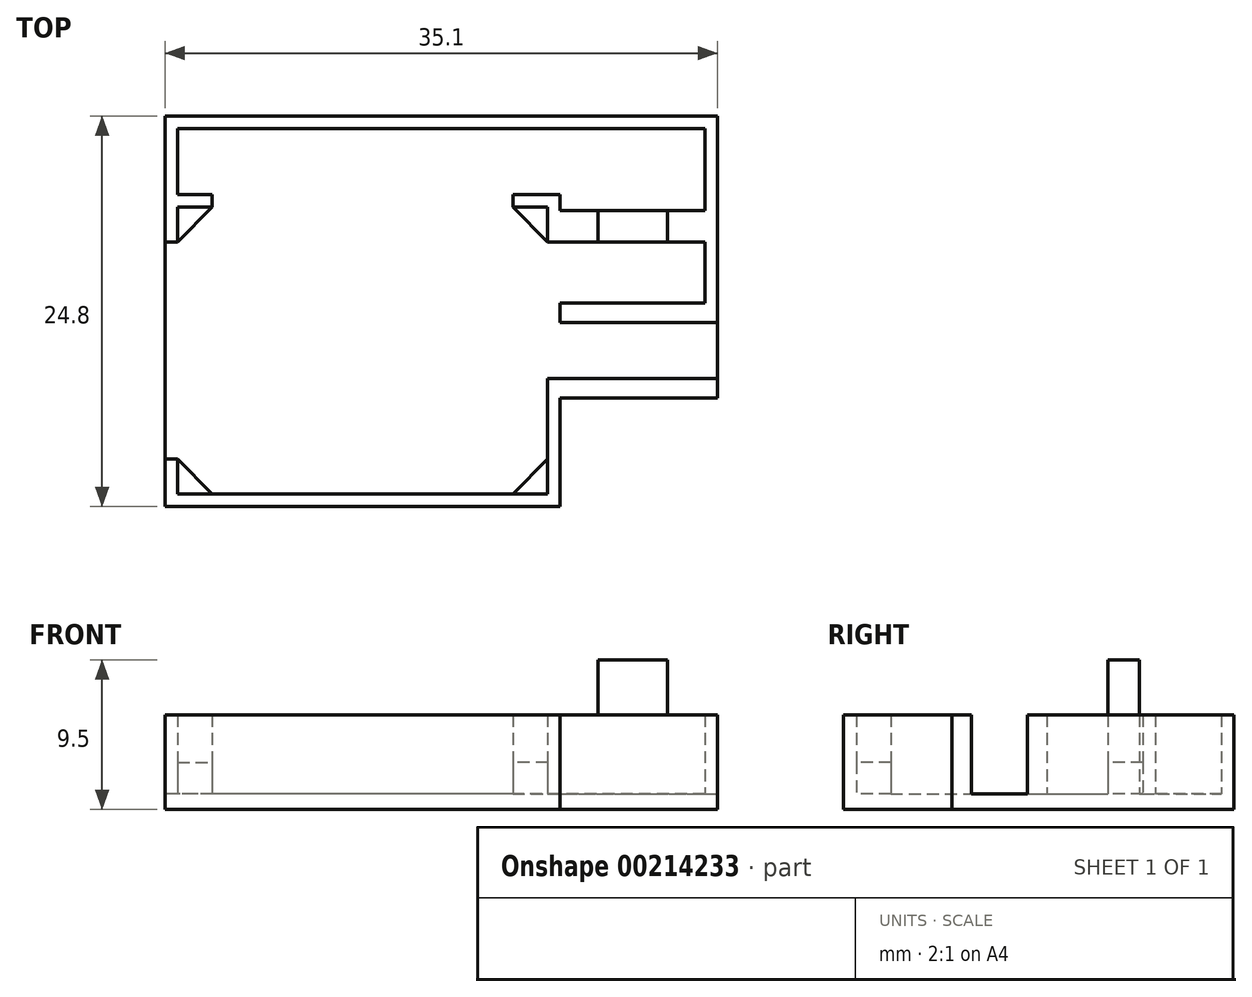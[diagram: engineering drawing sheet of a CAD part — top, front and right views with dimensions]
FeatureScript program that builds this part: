
annotation { "Feature Type Name" : "Feature", "Feature Type Description" : "" }
export const myFeature = defineFeature(function(context is Context, id is Id, definition is map)
    precondition{}
    {
        {
            var Q0;
            Q0=qCreatedBy(makeId("Top.planeOp"),FACE);
            var sketch = newSketch(context, id + "F0", { "sketchPlane" : qUnion([Q0])});
            skLineSegment(sketch, "E0.bottom", {"start": v(23.18, -7.6) * mm, "end": v(-1.92, -7.6) * mm});
            skLineSegment(sketch, "E0.top", {"start": v(23.18, 12.2) * mm, "end": v(-1.92, 12.2) * mm});
            skLineSegment(sketch, "E0.left", {"start": v(23.18, -7.6) * mm, "end": v(23.18, 12.2) * mm});
            skLineSegment(sketch, "E0.right", {"start": v(-1.92, -7.6) * mm, "end": v(-1.92, -6.8) * mm});
            skPoint(sketch, "E0.middle", {"position": v(10.63, 2.3) * mm});
            skLineSegment(sketch, "E1.bottom", {"start": v(22.38, -6.8) * mm, "end": v(-1.12, -6.8) * mm});
            skLineSegment(sketch, "E1.top", {"start": v(22.38, 11.4) * mm, "end": v(-1.12, 11.4) * mm});
            skLineSegment(sketch, "E1.left", {"start": v(22.38, -6.8) * mm, "end": v(22.38, 11.4) * mm});
            skLineSegment(sketch, "E1.right", {"start": v(-1.12, -6.8) * mm, "end": v(-1.12, 11.4) * mm});
            skLineSegment(sketch, "E2", {"start": v(22.38, 9.2) * mm, "end": v(23.18, 9.2) * mm});
            skLineSegment(sketch, "E3.MirrorCS", {"start": v(22.38, -4.6) * mm, "end": v(23.18, -4.6) * mm});
            skLineSegment(sketch, "E4", {"start": v(-1.12, 9.2) * mm, "end": v(-1.92, 9.2) * mm});
            skPoint(sketch, "E5.MirrorCS.end.orphan", {"position": v(20.18, -7.6) * mm});
            skPoint(sketch, "E5.MirrorCS.start.orphan", {"position": v(20.18, -6.8) * mm});
            skPoint(sketch, "E6.MirrorCS.end.orphan", {"position": v(1.08, -7.6) * mm});
            skPoint(sketch, "E6.MirrorCS.start.orphan", {"position": v(1.08, -6.8) * mm});
            skPoint(sketch, "E7.MirrorCS.end.orphan", {"position": v(1.08, 12.2) * mm});
            skPoint(sketch, "E7.MirrorCS.start.orphan", {"position": v(1.08, 11.4) * mm});
            skPoint(sketch, "E8.end.orphan", {"position": v(20.18, 12.2) * mm});
            skPoint(sketch, "E8.start.orphan", {"position": v(20.18, 11.4) * mm});
            skLineSegment(sketch, "E9", {"start": v(20.18, 11.4) * mm, "end": v(22.38, 9.2) * mm});
            skLineSegment(sketch, "E10", {"start": v(-1.12, -4.6) * mm, "end": v(1.08, -6.8) * mm});
            skLineSegment(sketch, "E11", {"start": v(-1.12, 9.2) * mm, "end": v(1.08, 11.4) * mm});
            skLineSegment(sketch, "E12", {"start": v(22.38, -4.6) * mm, "end": v(20.18, -6.8) * mm});
            skLineSegment(sketch, "E13", {"start": v(1.08, -7.6) * mm, "end": v(1.08, -6.8) * mm});
            skLineSegment(sketch, "E14", {"start": v(20.18, -7.6) * mm, "end": v(20.18, -6.8) * mm});
            skLineSegment(sketch, "E15", {"start": v(1.08, 11.4) * mm, "end": v(1.08, 12.2) * mm});
            skLineSegment(sketch, "E16", {"start": v(20.18, 11.4) * mm, "end": v(20.18, 12.2) * mm});
            skLineSegment(sketch, "E17", {"start": v(10.63, 4.67) * mm, "end": v(10.63, -1.07) * mm, "construction": true});
            skLineSegment(sketch, "E18.MirrorCS", {"start": v(33.18, 12.2) * mm, "end": v(29.93, 12.2) * mm});
            skLineSegment(sketch, "E19.MirrorCS", {"start": v(25.63, 5.32) * mm, "end": v(29.93, 5.32) * mm});
            skLineSegment(sketch, "E20.MirrorCS", {"start": v(23.18, 4.07) * mm, "end": v(32.38, 4.07) * mm});
            skLineSegment(sketch, "E21.MirrorCS", {"start": v(23.18, 0.52) * mm, "end": v(32.38, 0.52) * mm});
            skLineSegment(sketch, "E22.MirrorCS", {"start": v(23.18, -0.73) * mm, "end": v(32.38, -0.73) * mm});
            skLineSegment(sketch, "E23.MirrorCS", {"start": v(32.38, 4.07) * mm, "end": v(33.18, 4.07) * mm});
            skLineSegment(sketch, "E24.MirrorCS", {"start": v(32.38, 0.52) * mm, "end": v(33.18, 0.52) * mm});
            skLineSegment(sketch, "E25.MirrorCS", {"start": v(33.18, 0.52) * mm, "end": v(33.18, 4.07) * mm});
            skLineSegment(sketch, "E26.MirrorCS", {"start": v(33.18, -0.73) * mm, "end": v(33.18, 5.32) * mm});
            skLineSegment(sketch, "E27", {"start": v(33.18, 12.2) * mm, "end": v(33.18, 5.32) * mm});
            skLineSegment(sketch, "E28", {"start": v(33.18, -0.73) * mm, "end": v(32.38, -0.73) * mm});
            skLineSegment(sketch, "E29.trimOffspring", {"start": v(-1.92, 9.2) * mm, "end": v(-1.92, 12.2) * mm});
            skLineSegment(sketch, "E30", {"start": v(-1.92, -6.8) * mm, "end": v(-1.92, 9.2) * mm});
            skLineSegment(sketch, "E31", {"start": v(-1.12, -4.6) * mm, "end": v(-1.92, -4.6) * mm});
            skLineSegment(sketch, "E32", {"start": v(29.93, 12.2) * mm, "end": v(29.93, 5.32) * mm});
            skLineSegment(sketch, "E33", {"start": v(25.63, 5.32) * mm, "end": v(25.63, 12.2) * mm});
            skLineSegment(sketch, "E34", {"start": v(25.63, 5.32) * mm, "end": v(23.18, 5.32) * mm});
            skLineSegment(sketch, "E35", {"start": v(32.38, -0.73) * mm, "end": v(32.38, 12.2) * mm});
            skLineSegment(sketch, "E36", {"start": v(29.93, 5.32) * mm, "end": v(32.38, 5.32) * mm});
            skLineSegment(sketch, "E37", {"start": v(32.38, 5.32) * mm, "end": v(33.18, 5.32) * mm});
            skLineSegment(sketch, "E38", {"start": v(23.18, 11.2) * mm, "end": v(25.63, 11.2) * mm});
            skLineSegment(sketch, "E39", {"start": v(23.18, 9.2) * mm, "end": v(25.63, 9.2) * mm});
            skLineSegment(sketch, "E40.trimOffspring", {"start": v(25.63, 12.2) * mm, "end": v(23.18, 12.2) * mm});
            skLineSegment(sketch, "E41", {"start": v(25.63, 11.2) * mm, "end": v(29.93, 11.2) * mm});
            skLineSegment(sketch, "E42", {"start": v(25.63, 9.2) * mm, "end": v(29.93, 9.2) * mm});
            skLineSegment(sketch, "E43", {"start": v(25.63, 12.2) * mm, "end": v(29.93, 12.2) * mm});
            skLineSegment(sketch, "E44.0", {"start": v(23.18, 17.2) * mm, "end": v(-1.92, 17.2) * mm});
            skLineSegment(sketch, "E44.1", {"start": v(25.63, 17.2) * mm, "end": v(23.18, 17.2) * mm});
            skLineSegment(sketch, "E44.2", {"start": v(25.63, 17.2) * mm, "end": v(29.93, 17.2) * mm});
            skLineSegment(sketch, "E44.3", {"start": v(33.18, 17.2) * mm, "end": v(29.93, 17.2) * mm});
            skLineSegment(sketch, "E45", {"start": v(-1.92, 17.2) * mm, "end": v(-1.92, 12.2) * mm});
            skLineSegment(sketch, "E46.0", {"start": v(-1.12, 16.4) * mm, "end": v(-1.12, 12.2) * mm});
            skLineSegment(sketch, "E46.1", {"start": v(32.38, 16.4) * mm, "end": v(29.93, 16.4) * mm});
            skLineSegment(sketch, "E46.2", {"start": v(25.63, 16.4) * mm, "end": v(29.93, 16.4) * mm});
            skLineSegment(sketch, "E46.3", {"start": v(25.63, 16.4) * mm, "end": v(23.18, 16.4) * mm});
            skLineSegment(sketch, "E46.4", {"start": v(23.18, 16.4) * mm, "end": v(-1.12, 16.4) * mm});
            skLineSegment(sketch, "E47", {"start": v(33.18, 17.2) * mm, "end": v(33.18, 12.2) * mm});
            skLineSegment(sketch, "E48", {"start": v(32.38, 12.2) * mm, "end": v(32.38, 16.4) * mm});
            skLineSegment(sketch, "E49", {"start": v(23.18, 0.52) * mm, "end": v(22.38, 0.52) * mm});
            skLineSegment(sketch, "E50", {"start": v(29.93, 9.2) * mm, "end": v(32.38, 9.2) * mm});
            skLineSegment(sketch, "E51", {"start": v(29.93, 11.2) * mm, "end": v(32.38, 11.2) * mm});
            skSolve(sketch);
        }
        {
            var Q0;
            {var subQ0=sQuery(id+"F0.wireOp",EDGE,"E4");Q0=makeQuery(id+"F0.imprint","IMPRINT",FACE,{"disambiguationData":[TD([[makeQuery(id+"F0.imprint","IMPRINT",EDGE,{"derivedFrom":subQ0}),-1.0]])]});}
            var Q1;
            {var subQ3=sQuery(id+"F0.wireOp",EDGE,"E11");Q1=makeQuery(id+"F0.imprint","IMPRINT",FACE,{"disambiguationData":[TD([[makeQuery(id+"F0.imprint","IMPRINT",EDGE,{"derivedFrom":subQ3}),1.0]])]});}
            var Q2;
            {var subQ0=sQuery(id+"F0.wireOp",EDGE,"E15");Q2=makeQuery(id+"F0.imprint","IMPRINT",FACE,{"disambiguationData":[TD([[makeQuery(id+"F0.imprint","IMPRINT",EDGE,{"derivedFrom":subQ0}),-1.0]])]});}
            var Q3;
            {var subQ3=sQuery(id+"F0.wireOp",EDGE,"E9");Q3=makeQuery(id+"F0.imprint","IMPRINT",FACE,{"disambiguationData":[TD([[makeQuery(id+"F0.imprint","IMPRINT",EDGE,{"derivedFrom":subQ3}),-1.0]])]});}
            var Q4;
            {var subQ0=sQuery(id+"F0.wireOp",EDGE,"E4");Q4=makeQuery(id+"F0.imprint","IMPRINT",FACE,{"disambiguationData":[TD([[makeQuery(id+"F0.imprint","IMPRINT",EDGE,{"derivedFrom":subQ0}),1.0]])]});}
            var Q5;
            {var subQ6=sQuery(id+"F0.wireOp",EDGE,"E0.right");Q5=makeQuery(id+"F0.imprint","IMPRINT",FACE,{"disambiguationData":[TD([[makeQuery(id+"F0.imprint","IMPRINT",EDGE,{"derivedFrom":subQ6}),-1.0]])]});}
            var Q6;
            {var subQ3=sQuery(id+"F0.wireOp",EDGE,"E10");Q6=makeQuery(id+"F0.imprint","IMPRINT",FACE,{"disambiguationData":[TD([[makeQuery(id+"F0.imprint","IMPRINT",EDGE,{"derivedFrom":subQ3}),-1.0]])]});}
            var Q7;
            {var subQ0=sQuery(id+"F0.wireOp",EDGE,"E13");Q7=makeQuery(id+"F0.imprint","IMPRINT",FACE,{"disambiguationData":[TD([[makeQuery(id+"F0.imprint","IMPRINT",EDGE,{"derivedFrom":subQ0}),-1.0]])]});}
            var Q8;
            {var subQ5=sQuery(id+"F0.wireOp",EDGE,"E3.MirrorCS");Q8=makeQuery(id+"F0.imprint","IMPRINT",FACE,{"disambiguationData":[TD([[makeQuery(id+"F0.imprint","IMPRINT",EDGE,{"derivedFrom":subQ5}),-1.0]])]});}
            var Q9;
            {var subQ3=sQuery(id+"F0.wireOp",EDGE,"E12");Q9=makeQuery(id+"F0.imprint","IMPRINT",FACE,{"disambiguationData":[TD([[makeQuery(id+"F0.imprint","IMPRINT",EDGE,{"derivedFrom":subQ3}),1.0]])]});}
            var Q10;
            {var subQ4=sQuery(id+"F0.wireOp",EDGE,"E2");Q10=makeQuery(id+"F0.imprint","IMPRINT",FACE,{"disambiguationData":[TD([[makeQuery(id+"F0.imprint","IMPRINT",EDGE,{"derivedFrom":subQ4}),-1.0]])]});}
            var Q11;
            {var subQ3=sQuery(id+"F0.wireOp",EDGE,"E9");Q11=makeQuery(id+"F0.imprint","IMPRINT",FACE,{"disambiguationData":[TD([[makeQuery(id+"F0.imprint","IMPRINT",EDGE,{"derivedFrom":subQ3}),1.0]])]});}
            var Q12;
            {var subQ5=sQuery(id+"F0.wireOp",EDGE,"E2");Q12=makeQuery(id+"F0.imprint","IMPRINT",FACE,{"disambiguationData":[TD([[makeQuery(id+"F0.imprint","IMPRINT",EDGE,{"derivedFrom":subQ5}),1.0]])]});}
            var Q13;
            {var subQ2=sQuery(id+"F0.wireOp",EDGE,"E38");Q13=makeQuery(id+"F0.imprint","IMPRINT",FACE,{"disambiguationData":[TD([[makeQuery(id+"F0.imprint","IMPRINT",EDGE,{"derivedFrom":subQ2}),1.0]])]});}
            var Q14;
            {var subQ2=sQuery(id+"F0.wireOp",EDGE,"E38");Q14=makeQuery(id+"F0.imprint","IMPRINT",FACE,{"disambiguationData":[TD([[makeQuery(id+"F0.imprint","IMPRINT",EDGE,{"derivedFrom":subQ2}),-1.0]])]});}
            var Q15;
            {var subQ0=sQuery(id+"F0.wireOp",EDGE,"E41");Q15=makeQuery(id+"F0.imprint","IMPRINT",FACE,{"disambiguationData":[TD([[makeQuery(id+"F0.imprint","IMPRINT",EDGE,{"derivedFrom":subQ0}),-1.0]])]});}
            var Q16;
            {var subQ2=sQuery(id+"F0.wireOp",EDGE,"E41");Q16=makeQuery(id+"F0.imprint","IMPRINT",FACE,{"disambiguationData":[TD([[makeQuery(id+"F0.imprint","IMPRINT",EDGE,{"derivedFrom":subQ2}),1.0]])]});}
            var Q17;
            {var subQ0=sQuery(id+"F0.wireOp",EDGE,"E36");Q17=makeQuery(id+"F0.imprint","IMPRINT",FACE,{"disambiguationData":[TD([[makeQuery(id+"F0.imprint","IMPRINT",EDGE,{"derivedFrom":subQ0}),1.0]])]});}
            var Q18;
            {var subQ0=sQuery(id+"F0.wireOp",EDGE,"E27");Q18=makeQuery(id+"F0.imprint","IMPRINT",FACE,{"disambiguationData":[TD([[makeQuery(id+"F0.imprint","IMPRINT",EDGE,{"derivedFrom":subQ0}),-1.0]])]});}
            var Q19;
            {var subQ0=sQuery(id+"F0.wireOp",EDGE,"E19.MirrorCS");Q19=makeQuery(id+"F0.imprint","IMPRINT",FACE,{"disambiguationData":[TD([[makeQuery(id+"F0.imprint","IMPRINT",EDGE,{"derivedFrom":subQ0}),1.0]])]});}
            var Q20;
            {var subQ2=sQuery(id+"F0.wireOp",EDGE,"E34");Q20=makeQuery(id+"F0.imprint","IMPRINT",FACE,{"disambiguationData":[TD([[makeQuery(id+"F0.imprint","IMPRINT",EDGE,{"derivedFrom":subQ2}),-1.0]])]});}
            var Q21;
            Q21=makeQuery(id+"F0.imprint","IMPRINT",FACE,{"disambiguationData":[TD([[makeQuery(id+"F0.imprint","IMPRINT",EDGE,{"derivedFrom":sQuery(id+"F0.wireOp",EDGE,"E19.MirrorCS")}),-1.0]])]});
            var Q22;
            {var subQ0=sQuery(id+"F0.wireOp",EDGE,"E20.MirrorCS");Q22=makeQuery(id+"F0.imprint","IMPRINT",FACE,{"disambiguationData":[TD([[makeQuery(id+"F0.imprint","IMPRINT",EDGE,{"derivedFrom":subQ0}),-1.0]])]});}
            var Q23;
            {var subQ0=sQuery(id+"F0.wireOp",EDGE,"E21.MirrorCS");Q23=makeQuery(id+"F0.imprint","IMPRINT",FACE,{"disambiguationData":[TD([[makeQuery(id+"F0.imprint","IMPRINT",EDGE,{"derivedFrom":subQ0}),-1.0]])]});}
            var Q24;
            {var subQ0=sQuery(id+"F0.wireOp",EDGE,"E24.MirrorCS");Q24=makeQuery(id+"F0.imprint","IMPRINT",FACE,{"disambiguationData":[TD([[makeQuery(id+"F0.imprint","IMPRINT",EDGE,{"derivedFrom":subQ0}),-1.0]])]});}
            var Q25;
            {var subQ0=sQuery(id+"F0.wireOp",EDGE,"E23.MirrorCS");Q25=makeQuery(id+"F0.imprint","IMPRINT",FACE,{"disambiguationData":[TD([[makeQuery(id+"F0.imprint","IMPRINT",EDGE,{"derivedFrom":subQ0}),-1.0]])]});}
            var Q26;
            {var subQ0=sQuery(id+"F0.wireOp",EDGE,"E23.MirrorCS");Q26=makeQuery(id+"F0.imprint","IMPRINT",FACE,{"disambiguationData":[TD([[makeQuery(id+"F0.imprint","IMPRINT",EDGE,{"derivedFrom":subQ0}),1.0]])]});}
            var Q27;
            Q27=makeQuery(id+"F0.imprint","IMPRINT",FACE,{"disambiguationData":[TD([[makeQuery(id+"F0.imprint","IMPRINT",EDGE,{"derivedFrom":sQuery(id+"F0.wireOp",EDGE,"E44.0")}),1.0]])]});
            var Q28;
            {var subQ2=sQuery(id+"F0.wireOp",EDGE,"E40.trimOffspring");Q28=makeQuery(id+"F0.imprint","IMPRINT",FACE,{"disambiguationData":[TD([[makeQuery(id+"F0.imprint","IMPRINT",EDGE,{"derivedFrom":subQ2}),-1.0]])]});}
            var Q29;
            {var subQ0=sQuery(id+"F0.wireOp",EDGE,"E3.MirrorCS");Q29=makeQuery(id+"F0.imprint","IMPRINT",FACE,{"disambiguationData":[TD([[makeQuery(id+"F0.imprint","IMPRINT",EDGE,{"derivedFrom":subQ0}),1.0]])]});}
            var Q30;
            {var subQ3=sQuery(id+"F0.wireOp",EDGE,"E50");Q30=makeQuery(id+"F0.imprint","IMPRINT",FACE,{"disambiguationData":[TD([[makeQuery(id+"F0.imprint","IMPRINT",EDGE,{"derivedFrom":subQ3}),1.0]])]});}
            var Q31;
            Q31=makeQuery(id+"F0.imprint","IMPRINT",FACE,{"disambiguationData":[TD([[makeQuery(id+"F0.imprint","IMPRINT",EDGE,{"derivedFrom":sQuery(id+"F0.wireOp",EDGE,"587ad5e2-a71c-4068-8914-0ef3fa984659.0")}),-1.0]])]});
            var Q32;
            {var subQ5=sQuery(id+"F0.wireOp",EDGE,"E51");Q32=makeQuery(id+"F0.imprint","IMPRINT",FACE,{"disambiguationData":[TD([[makeQuery(id+"F0.imprint","IMPRINT",EDGE,{"derivedFrom":subQ5}),1.0]])]});}
            extrude(context, id + "F1", {"entities" : qUnion([Q0, Q1, Q2, Q3, Q4, Q5, Q6, Q7, Q8, Q9, Q10, Q11, Q12, Q13, Q14, Q15, Q16, Q17, Q18, Q19, Q20, Q21, Q22, Q23, Q24, Q25, Q26, Q27, Q28, Q29, Q30, Q31, Q32]), "oppositeDirection" : true, "depth" : 1 * mm});
        }
        {
            var Q0;
            {var subQ3=sQuery(id+"F0.wireOp",EDGE,"E10");Q0=makeQuery(id+"F0.imprint","IMPRINT",FACE,{"disambiguationData":[TD([[makeQuery(id+"F0.imprint","IMPRINT",EDGE,{"derivedFrom":subQ3}),-1.0]])]});}
            var Q1;
            {var subQ3=sQuery(id+"F0.wireOp",EDGE,"E12");Q1=makeQuery(id+"F0.imprint","IMPRINT",FACE,{"disambiguationData":[TD([[makeQuery(id+"F0.imprint","IMPRINT",EDGE,{"derivedFrom":subQ3}),1.0]])]});}
            var Q2;
            {var subQ3=sQuery(id+"F0.wireOp",EDGE,"E9");Q2=makeQuery(id+"F0.imprint","IMPRINT",FACE,{"disambiguationData":[TD([[makeQuery(id+"F0.imprint","IMPRINT",EDGE,{"derivedFrom":subQ3}),1.0]])]});}
            var Q3;
            {var subQ3=sQuery(id+"F0.wireOp",EDGE,"E11");Q3=makeQuery(id+"F0.imprint","IMPRINT",FACE,{"disambiguationData":[TD([[makeQuery(id+"F0.imprint","IMPRINT",EDGE,{"derivedFrom":subQ3}),1.0]])]});}
            extrude(context, id + "F2", {"entities" : qUnion([Q0, Q1, Q2, Q3]), "operationType" : NewBodyOperationType.ADD, "depth" : 2 * mm});
        }
        {
            var Q0;
            {var subQ5=sQuery(id+"F0.wireOp",EDGE,"E0.right");Q0=makeQuery(id+"F0.imprint","IMPRINT",FACE,{"disambiguationData":[TD([[makeQuery(id+"F0.imprint","IMPRINT",EDGE,{"derivedFrom":subQ5}),-1.0]])]});}
            var Q1;
            {var subQ4=sQuery(id+"F0.wireOp",EDGE,"E4");Q1=makeQuery(id+"F0.imprint","IMPRINT",FACE,{"disambiguationData":[TD([[makeQuery(id+"F0.imprint","IMPRINT",EDGE,{"derivedFrom":subQ4}),-1.0]])]});}
            var Q2;
            {var subQ4=sQuery(id+"F0.wireOp",EDGE,"E3.MirrorCS");Q2=makeQuery(id+"F0.imprint","IMPRINT",FACE,{"disambiguationData":[TD([[makeQuery(id+"F0.imprint","IMPRINT",EDGE,{"derivedFrom":subQ4}),-1.0]])]});}
            var Q3;
            {var subQ9=sQuery(id+"F0.wireOp",EDGE,"E2");Q3=makeQuery(id+"F0.imprint","IMPRINT",FACE,{"disambiguationData":[TD([[makeQuery(id+"F0.imprint","IMPRINT",EDGE,{"derivedFrom":subQ9}),1.0]])]});}
            var Q4;
            Q4=makeQuery(id+"F0.imprint","IMPRINT",FACE,{"disambiguationData":[TD([[makeQuery(id+"F0.imprint","IMPRINT",EDGE,{"derivedFrom":sQuery(id+"F0.wireOp",EDGE,"E44.0")}),1.0]])]});
            var Q5;
            {var subQ5=sQuery(id+"F0.wireOp",EDGE,"E27");Q5=makeQuery(id+"F0.imprint","IMPRINT",FACE,{"disambiguationData":[TD([[makeQuery(id+"F0.imprint","IMPRINT",EDGE,{"derivedFrom":subQ5}),-1.0]])]});}
            var Q6;
            {var subQ0=sQuery(id+"F0.wireOp",EDGE,"E23.MirrorCS");Q6=makeQuery(id+"F0.imprint","IMPRINT",FACE,{"disambiguationData":[TD([[makeQuery(id+"F0.imprint","IMPRINT",EDGE,{"derivedFrom":subQ0}),1.0]])]});}
            var Q7;
            {var subQ0=sQuery(id+"F0.wireOp",EDGE,"E24.MirrorCS");Q7=makeQuery(id+"F0.imprint","IMPRINT",FACE,{"disambiguationData":[TD([[makeQuery(id+"F0.imprint","IMPRINT",EDGE,{"derivedFrom":subQ0}),-1.0]])]});}
            var Q8;
            {var subQ0=sQuery(id+"F0.wireOp",EDGE,"E21.MirrorCS");Q8=makeQuery(id+"F0.imprint","IMPRINT",FACE,{"disambiguationData":[TD([[makeQuery(id+"F0.imprint","IMPRINT",EDGE,{"derivedFrom":subQ0}),-1.0]])]});}
            var Q9;
            {var subQ0=sQuery(id+"F0.wireOp",EDGE,"E3.MirrorCS");Q9=makeQuery(id+"F0.imprint","IMPRINT",FACE,{"disambiguationData":[TD([[makeQuery(id+"F0.imprint","IMPRINT",EDGE,{"derivedFrom":subQ0}),1.0]])]});}
            var Q10;
            Q10=makeQuery(id+"F0.imprint","IMPRINT",FACE,{"disambiguationData":[TD([[makeQuery(id+"F0.imprint","IMPRINT",EDGE,{"derivedFrom":sQuery(id+"F0.wireOp",EDGE,"587ad5e2-a71c-4068-8914-0ef3fa984659.0")}),-1.0]])]});
            var Q11;
            {var subQ0=sQuery(id+"F0.wireOp",EDGE,"E41");Q11=makeQuery(id+"F0.imprint","IMPRINT",FACE,{"disambiguationData":[TD([[makeQuery(id+"F0.imprint","IMPRINT",EDGE,{"derivedFrom":subQ0}),-1.0]])]});}
            var Q12;
            {var subQ2=sQuery(id+"F0.wireOp",EDGE,"E38");Q12=makeQuery(id+"F0.imprint","IMPRINT",FACE,{"disambiguationData":[TD([[makeQuery(id+"F0.imprint","IMPRINT",EDGE,{"derivedFrom":subQ2}),-1.0]])]});}
            var Q13;
            {var subQ2=sQuery(id+"F0.wireOp",EDGE,"E50");Q13=makeQuery(id+"F0.imprint","IMPRINT",FACE,{"disambiguationData":[TD([[makeQuery(id+"F0.imprint","IMPRINT",EDGE,{"derivedFrom":subQ2}),1.0]])]});}
            var Q14;
            Q14=makeQuery(id+"F0.imprint","IMPRINT",FACE,{"disambiguationData":[TD([[makeQuery(id+"F0.imprint","IMPRINT",EDGE,{"derivedFrom":sQuery(id+"F0.wireOp",EDGE,"E19.MirrorCS")}),-1.0]])]});
            var Q15;
            {var subQ0=sQuery(id+"F0.wireOp",EDGE,"E13");Q15=makeQuery(id+"F0.imprint","IMPRINT",FACE,{"disambiguationData":[TD([[makeQuery(id+"F0.imprint","IMPRINT",EDGE,{"derivedFrom":subQ0}),-1.0]])]});}
            extrude(context, id + "F3", {"entities" : qUnion([Q0, Q1, Q2, Q3, Q4, Q5, Q6, Q7, Q8, Q9, Q10, Q11, Q12, Q13, Q14, Q15]), "operationType" : NewBodyOperationType.ADD, "depth" : 5 * mm});
        }
        {
            var Q0;
            Q0=makeQuery(id+"F3.opExtrude","CAP_FACE",FACE,{"disambiguationData":[OSD([sQuery(id+"F0.wireOp",EDGE,"E0.top"),sQuery(id+"F0.wireOp",EDGE,"E0.left"),sQuery(id+"F0.wireOp",EDGE,"E1.top"),sQuery(id+"F0.wireOp",EDGE,"E1.left"),sQuery(id+"F0.wireOp",EDGE,"E1.right"),sQuery(id+"F0.wireOp",EDGE,"E2"),sQuery(id+"F0.wireOp",EDGE,"E4"),sQuery(id+"F0.wireOp",EDGE,"E15"),sQuery(id+"F0.wireOp",EDGE,"E16"),sQuery(id+"F0.wireOp",EDGE,"E19.MirrorCS"),sQuery(id+"F0.wireOp",EDGE,"E20.MirrorCS"),sQuery(id+"F0.wireOp",EDGE,"E23.MirrorCS"),sQuery(id+"F0.wireOp",EDGE,"E26.MirrorCS"),sQuery(id+"F0.wireOp",EDGE,"E27"),sQuery(id+"F0.wireOp",EDGE,"E29.trimOffspring"),sQuery(id+"F0.wireOp",EDGE,"E34"),sQuery(id+"F0.wireOp",EDGE,"E35"),sQuery(id+"F0.wireOp",EDGE,"E36"),sQuery(id+"F0.wireOp",EDGE,"E38"),sQuery(id+"F0.wireOp",EDGE,"E39"),sQuery(id+"F0.wireOp",EDGE,"E41"),sQuery(id+"F0.wireOp",EDGE,"E42"),sQuery(id+"F0.wireOp",EDGE,"E44.0"),sQuery(id+"F0.wireOp",EDGE,"E44.1"),sQuery(id+"F0.wireOp",EDGE,"E44.2"),sQuery(id+"F0.wireOp",EDGE,"E44.3"),sQuery(id+"F0.wireOp",EDGE,"E45"),sQuery(id+"F0.wireOp",EDGE,"E46.0"),sQuery(id+"F0.wireOp",EDGE,"E46.1"),sQuery(id+"F0.wireOp",EDGE,"E46.2"),sQuery(id+"F0.wireOp",EDGE,"E46.3"),sQuery(id+"F0.wireOp",EDGE,"E46.4"),sQuery(id+"F0.wireOp",EDGE,"E47"),sQuery(id+"F0.wireOp",EDGE,"E48"),sQuery(id+"F0.wireOp",EDGE,"E50"),sQuery(id+"F0.wireOp",EDGE,"E51")])],"isStart":false});
            var sketch = newSketch(context, id + "F4", { "sketchPlane" : qUnion([Q0])});
            skPoint(sketch, "E52", {"position": v(27.78, 10.2) * mm});
            skLineSegment(sketch, "E53.bottom", {"start": v(29.98, 9.2) * mm, "end": v(25.58, 9.2) * mm});
            skLineSegment(sketch, "E53.top", {"start": v(29.98, 11.2) * mm, "end": v(25.58, 11.2) * mm});
            skLineSegment(sketch, "E53.left", {"start": v(29.98, 9.2) * mm, "end": v(29.98, 11.2) * mm});
            skLineSegment(sketch, "E53.right", {"start": v(25.58, 9.2) * mm, "end": v(25.58, 11.2) * mm});
            skLineSegment(sketch, "E54.bottom", {"start": v(29.98, 11.2) * mm, "end": v(32.38, 11.2) * mm});
            skLineSegment(sketch, "E54.top", {"start": v(29.98, 9.2) * mm, "end": v(32.38, 9.2) * mm});
            skLineSegment(sketch, "E54.left", {"start": v(29.98, 11.2) * mm, "end": v(29.98, 9.2) * mm});
            skLineSegment(sketch, "E54.right", {"start": v(32.38, 11.2) * mm, "end": v(32.38, 9.2) * mm});
            skLineSegment(sketch, "E55.bottom", {"start": v(25.58, 11.2) * mm, "end": v(23.18, 11.2) * mm});
            skLineSegment(sketch, "E55.top", {"start": v(25.58, 9.2) * mm, "end": v(23.18, 9.2) * mm});
            skLineSegment(sketch, "E55.left", {"start": v(25.58, 11.2) * mm, "end": v(25.58, 9.2) * mm});
            skLineSegment(sketch, "E55.right", {"start": v(23.18, 11.2) * mm, "end": v(23.18, 9.2) * mm});
            skLineSegment(sketch, "E56", {"start": v(31.98, 11.2) * mm, "end": v(31.98, 9.2) * mm});
            skLineSegment(sketch, "E57", {"start": v(23.58, 11.2) * mm, "end": v(23.58, 9.2) * mm});
            skSolve(sketch);
        }
        {
            var Q0;
            {var subQ0=sQuery(id+"F4.wireOp",EDGE,"E54.left");Q0=makeQuery(id+"F4.imprint","IMPRINT",FACE,{"disambiguationData":[TD([[makeQuery(id+"F4.imprint","IMPRINT",EDGE,{"derivedFrom":subQ0}),1.0]])]});}
            var Q1;
            {var subQ0=sQuery(id+"F4.wireOp",EDGE,"E55.left");Q1=makeQuery(id+"F4.imprint","IMPRINT",FACE,{"disambiguationData":[TD([[makeQuery(id+"F4.imprint","IMPRINT",EDGE,{"derivedFrom":subQ0}),-1.0]])]});}
            var Q2;
            Q2=makeQuery(id+"F4.imprint","IMPRINT",FACE,{"disambiguationData":[TD([[makeQuery(id+"F4.imprint","IMPRINT",EDGE,{"derivedFrom":sQuery(id+"F4.wireOp",EDGE,"E53.bottom")}),1.0]])]});
            extrude(context, id + "F5", {"entities" : qUnion([Q0, Q1, Q2]), "operationType" : NewBodyOperationType.ADD, "depth" : 1.5 * mm});
        }
        {
            var Q0;
            Q0=makeQuery(id+"F5.opExtrude","CAP_FACE",FACE,{"disambiguationData":[OSD([sQuery(id+"F4.wireOp",EDGE,"E53.bottom"),sQuery(id+"F4.wireOp",EDGE,"E53.top"),sQuery(id+"F4.wireOp",EDGE,"E54.bottom"),sQuery(id+"F4.wireOp",EDGE,"E54.top"),sQuery(id+"F4.wireOp",EDGE,"E54.right"),sQuery(id+"F4.wireOp",EDGE,"E55.bottom"),sQuery(id+"F4.wireOp",EDGE,"E55.top"),sQuery(id+"F4.wireOp",EDGE,"E55.right")])],"isStart":false});
            var sketch = newSketch(context, id + "F6", { "sketchPlane" : qUnion([Q0])});
            skLineSegment(sketch, "E58.bottom", {"start": v(23.58, 11.2) * mm, "end": v(25.58, 11.2) * mm});
            skLineSegment(sketch, "E58.top", {"start": v(23.58, 9.2) * mm, "end": v(25.58, 9.2) * mm});
            skLineSegment(sketch, "E58.left", {"start": v(23.58, 11.2) * mm, "end": v(23.58, 9.2) * mm});
            skLineSegment(sketch, "E58.right", {"start": v(25.58, 11.2) * mm, "end": v(25.58, 9.2) * mm});
            skLineSegment(sketch, "E59.bottom", {"start": v(31.98, 11.2) * mm, "end": v(29.98, 11.2) * mm});
            skLineSegment(sketch, "E59.top", {"start": v(31.98, 9.2) * mm, "end": v(29.98, 9.2) * mm});
            skLineSegment(sketch, "E59.left", {"start": v(31.98, 11.2) * mm, "end": v(31.98, 9.2) * mm});
            skLineSegment(sketch, "E59.right", {"start": v(29.98, 11.2) * mm, "end": v(29.98, 9.2) * mm});
            skSolve(sketch);
        }
        {
            var Q0;
            {var subQ0=sQuery(id+"F6.wireOp",EDGE,"E58.right");Q0=makeQuery(id+"F6.imprint","IMPRINT",FACE,{"disambiguationData":[TD([[makeQuery(id+"F6.imprint","IMPRINT",EDGE,{"derivedFrom":subQ0}),-1.0]])]});}
            var Q1;
            {var subQ0=sQuery(id+"F6.wireOp",EDGE,"E59.right");Q1=makeQuery(id+"F6.imprint","IMPRINT",FACE,{"disambiguationData":[TD([[makeQuery(id+"F6.imprint","IMPRINT",EDGE,{"derivedFrom":subQ0}),1.0]])]});}
            extrude(context, id + "F7", {"entities" : qUnion([Q0, Q1]), "operationType" : NewBodyOperationType.ADD, "depth" : 2 * mm});
        }
    });
